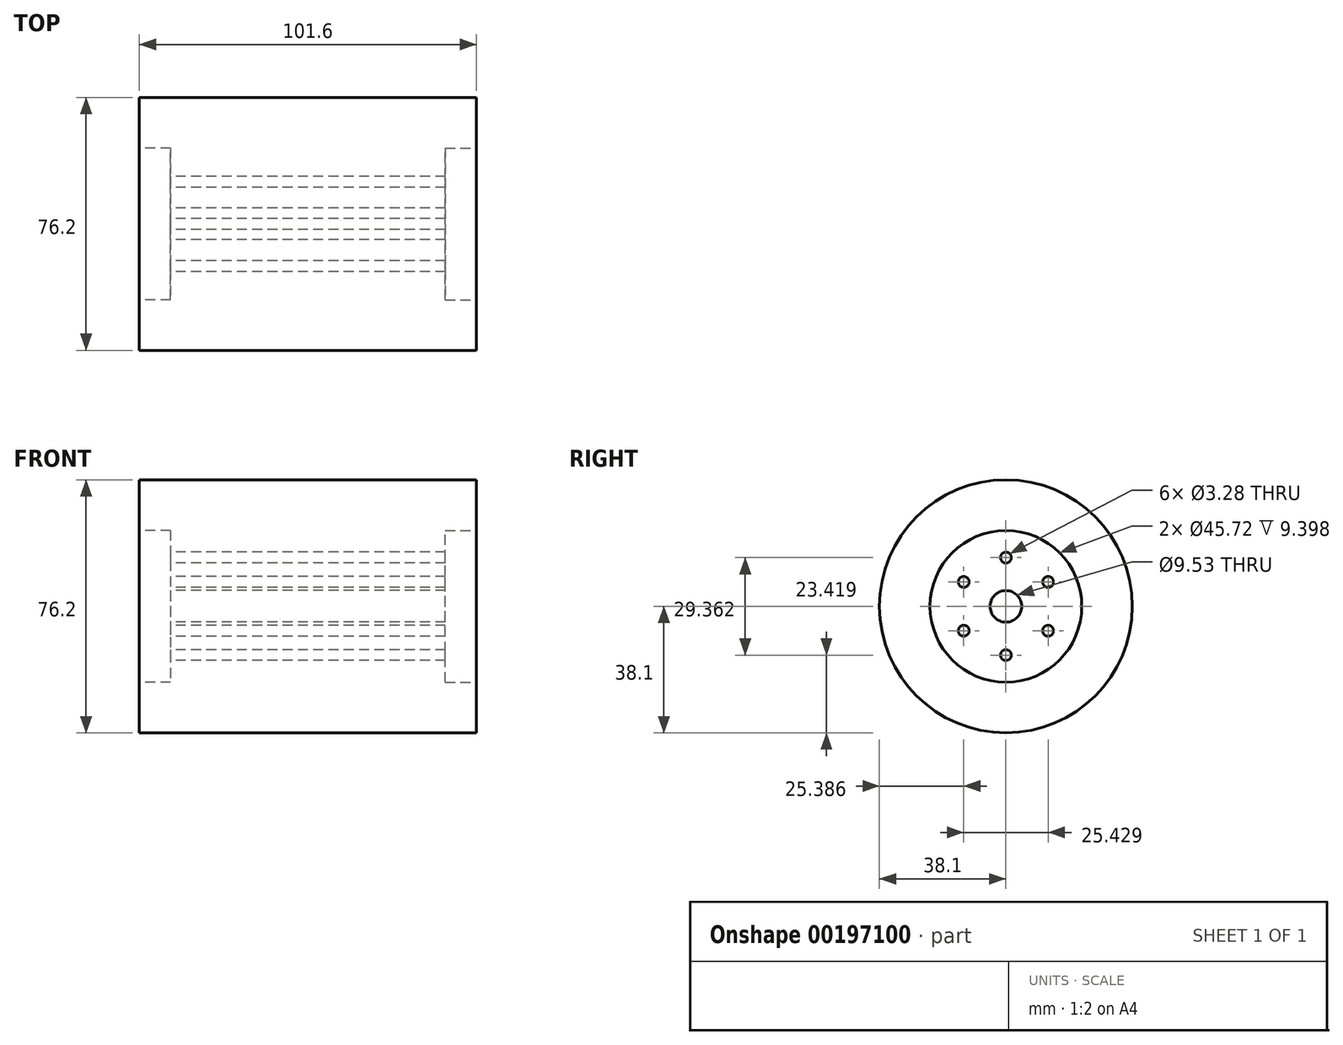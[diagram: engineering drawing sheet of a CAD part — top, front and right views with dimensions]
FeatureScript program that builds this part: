
annotation { "Feature Type Name" : "Feature", "Feature Type Description" : "" }
export const myFeature = defineFeature(function(context is Context, id is Id, definition is map)
    precondition{}
    {
        {
            var Q0;
            Q0=qCreatedBy(makeId("Right.planeOp"),FACE);
            var sketch = newSketch(context, id + "F0", { "sketchPlane" : qUnion([Q0])});
            skCircle(sketch, "E0", {"center": v(0, 0) * mm, "radius": 38.1 * mm});
            skSolve(sketch);
        }
        {
            var Q0;
            Q0 = qSketchRegion(id + "F0", true);
            extrude(context, id + "F1", {"entities" : qUnion([Q0]), "endBound" : BoundingType.SYMMETRIC, "depth" : 101.6 * mm});
        }
        {
            var Q0;
            Q0=makeQuery(id+"F1.opExtrude","CAP_FACE",FACE,{"disambiguationData":[OSD([sQuery(id+"F0.wireOp",EDGE,"E0")])],"isStart":false});
            var sketch = newSketch(context, id + "F2", { "sketchPlane" : qUnion([Q0])});
            skCircle(sketch, "E1", {"center": v(0, 0) * mm, "radius": 22.86 * mm});
            skSolve(sketch);
        }
        {
            var Q0;
            Q0 = qSketchRegion(id + "F2", true);
            extrude(context, id + "F3", {"entities" : qUnion([Q0]), "operationType" : NewBodyOperationType.REMOVE, "oppositeDirection" : true, "depth" : 9.4 * mm});
        }
        {
            var Q0;
            Q0=makeQuery(id+"F1.opExtrude","CAP_FACE",FACE,{"disambiguationData":[OSD([sQuery(id+"F0.wireOp",EDGE,"E0")])],"isStart":true});
            var sketch = newSketch(context, id + "F4", { "sketchPlane" : qUnion([Q0])});
            skCircle(sketch, "E2", {"center": v(0, 0) * mm, "radius": 22.86 * mm});
            skSolve(sketch);
        }
        {
            var Q0;
            Q0 = qSketchRegion(id + "F4", true);
            extrude(context, id + "F5", {"entities" : qUnion([Q0]), "operationType" : NewBodyOperationType.REMOVE, "oppositeDirection" : true, "depth" : 9.4 * mm});
        }
        {
            var Q0;
            Q0=makeQuery(id+"F1.opExtrude","CAP_FACE",FACE,{"disambiguationData":[OSD([sQuery(id+"F0.wireOp",EDGE,"E0")])],"isStart":true});
            var sketch = newSketch(context, id + "F6", { "sketchPlane" : qUnion([Q0])});
            skCircle(sketch, "E3", {"center": v(0, 0) * mm, "radius": 4.76 * mm});
            skSolve(sketch);
        }
        {
            var Q0;
            Q0 = qSketchRegion(id + "F6", true);
            extrude(context, id + "F7", {"entities" : qUnion([Q0]), "operationType" : NewBodyOperationType.REMOVE, "endBound" : BoundingType.THROUGH_ALL, "oppositeDirection" : true, "depth" : 25.4 * mm});
        }
        {
            var Q0;
            Q0=makeQuery(id+"F5.boolean.opBoolean","COPY",FACE,{"derivedFrom":makeQuery(id+"F5.opExtrude","CAP_FACE",FACE,{"disambiguationData":[OSD([sQuery(id+"F4.wireOp",EDGE,"E2")])],"isStart":false})});
            var sketch = newSketch(context, id + "F8", { "sketchPlane" : qUnion([Q0])});
            skCircle(sketch, "E4", {"center": v(0, 14.68) * mm, "radius": 1.64 * mm});
            skCircle(sketch, "E5.1.0", {"center": v(12.71, 7.34) * mm, "radius": 1.64 * mm});
            skCircle(sketch, "E5.2.0", {"center": v(12.71, -7.34) * mm, "radius": 1.64 * mm});
            skCircle(sketch, "E5.3.0", {"center": v(0, -14.68) * mm, "radius": 1.64 * mm});
            skCircle(sketch, "E5.4.0", {"center": v(-12.71, -7.34) * mm, "radius": 1.64 * mm});
            skCircle(sketch, "E5.5.0", {"center": v(-12.71, 7.34) * mm, "radius": 1.64 * mm});
            skPoint(sketch, "E5.center", {"position": v(0, 0) * mm});
            skLineSegment(sketch, "E5.anchor1", {"start": v(0, 0) * mm, "end": v(0, 14.68) * mm, "construction": true});
            skLineSegment(sketch, "E5.anchor2", {"start": v(0, 0) * mm, "end": v(-12.71, 7.34) * mm, "construction": true});
            skSolve(sketch);
        }
        {
            var Q0;
            Q0 = qSketchRegion(id + "F8", true);
            extrude(context, id + "F9", {"entities" : qUnion([Q0]), "operationType" : NewBodyOperationType.REMOVE, "endBound" : BoundingType.THROUGH_ALL, "oppositeDirection" : true, "depth" : 25.4 * mm});
        }
    });
